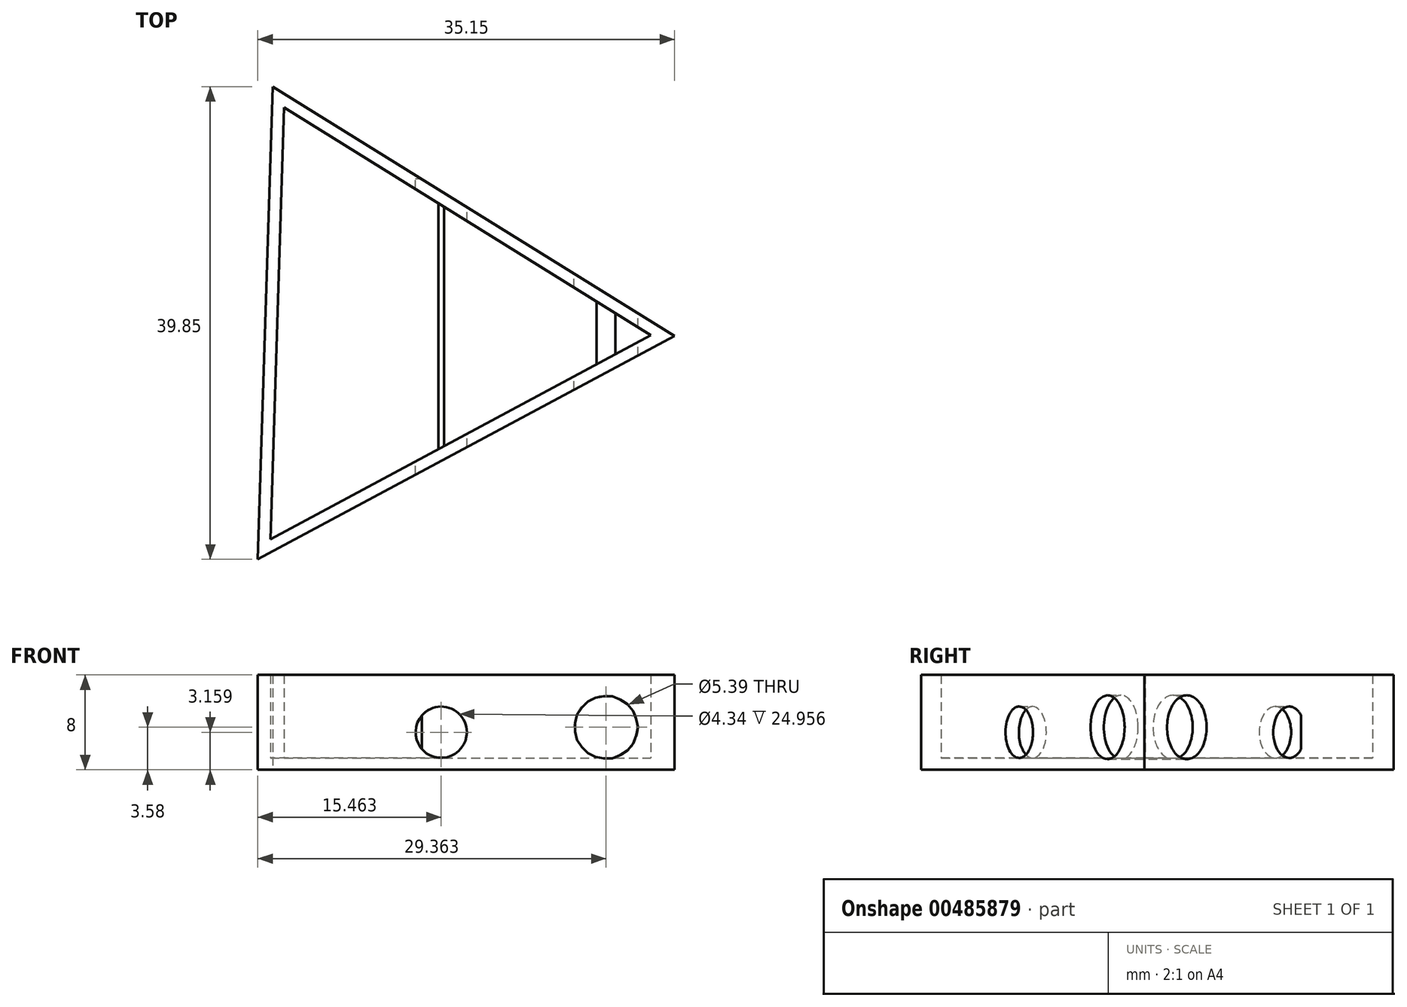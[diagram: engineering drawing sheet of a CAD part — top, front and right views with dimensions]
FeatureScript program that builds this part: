
annotation { "Feature Type Name" : "Feature", "Feature Type Description" : "" }
export const myFeature = defineFeature(function(context is Context, id is Id, definition is map)
    precondition{}
    {
        {
            var Q0;
            Q0=qCreatedBy(makeId("Top.planeOp"),FACE);
            var sketch = newSketch(context, id + "F0", { "sketchPlane" : qUnion([Q0])});
            skCircle(sketch, "E0.cCircle", {"center": v(0, 0) * mm, "radius": 11.5 * mm, "construction": true});
            skLineSegment(sketch, "E0.0", {"start": v(23, -0.73) * mm, "end": v(-12.14, -19.56) * mm});
            skLineSegment(sketch, "E0.1", {"start": v(-12.14, -19.56) * mm, "end": v(-10.87, 20.3) * mm});
            skLineSegment(sketch, "E0.2", {"start": v(-10.87, 20.3) * mm, "end": v(23, -0.73) * mm});
            skPoint(sketch, "E0.0.midPoint", {"position": v(5.44, -10.15) * mm});
            skSolve(sketch);
        }
        {
            var Q0;
            Q0=makeQuery(id+"F0.imprint","IMPRINT",FACE,{"disambiguationData":[TD([[makeQuery(id+"F0.imprint","IMPRINT",EDGE,{"derivedFrom":sQuery(id+"F0.wireOp",EDGE,"E0.0")}),-1.0]])]});
            extrude(context, id + "F1", {"entities" : qUnion([Q0]), "depth" : 8 * mm});
        }
        {
            var Q0;
            Q0=makeQuery(id+"F1.opExtrude","CAP_FACE",FACE,{"disambiguationData":[OSD([sQuery(id+"F0.wireOp",EDGE,"E0.0"),sQuery(id+"F0.wireOp",EDGE,"E0.1"),sQuery(id+"F0.wireOp",EDGE,"E0.2")])],"isStart":false});
            shell(context, id + "F2", {"entities" : qUnion([Q0]), "thickness" : 1 * mm});
        }
        {
            var Q0;
            Q0=qCreatedBy(makeId("Front.planeOp"),FACE);
            var sketch = newSketch(context, id + "F3", { "sketchPlane" : qUnion([Q0])});
            skCircle(sketch, "E1", {"center": v(17.22, 3.58) * mm, "radius": 2.7 * mm});
            skCircle(sketch, "E2", {"center": v(3.32, 3.16) * mm, "radius": 2.17 * mm});
            skSolve(sketch);
        }
        {
            var Q0;
            Q0=makeQuery(id+"F3.imprint","IMPRINT",FACE,{"disambiguationData":[TD([[makeQuery(id+"F3.imprint","IMPRINT",EDGE,{"derivedFrom":sQuery(id+"F3.wireOp",EDGE,"E2")}),1.0]])]});
            var Q1;
            Q1=makeQuery(id+"F3.imprint","IMPRINT",FACE,{"disambiguationData":[TD([[makeQuery(id+"F3.imprint","IMPRINT",EDGE,{"derivedFrom":sQuery(id+"F3.wireOp",EDGE,"E1")}),1.0]])]});
            extrude(context, id + "F4", {"entities" : qUnion([Q0, Q1]), "operationType" : NewBodyOperationType.REMOVE, "endBound" : BoundingType.SYMMETRIC, "depth" : 25 * mm});
        }
    });
